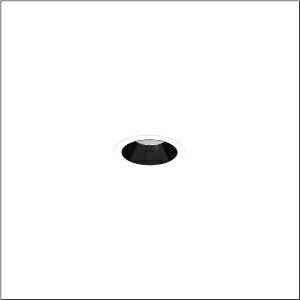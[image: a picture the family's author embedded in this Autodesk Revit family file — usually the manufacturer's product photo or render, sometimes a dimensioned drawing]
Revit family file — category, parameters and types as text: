
# Revit family: lunis_21_s_51db17ma91c
name_source: partatom
category: Lighting Fixtures
units: mm (PartAtom-declared; Revit-internal decimal feet)

## family parameters
Cut with Voids When Loaded = No
Host = Face
Light Source = No
Part Type = Normal
Room Calculation Point = No
Round Connector Dimension = Use Diameter
Shared = No

## types (1)
- --- (1 x LED, 830 lm, 5.9 W, 6500K)
    Apparent Load = 6 VA
    CIE Flux Codes = 97 100 100 100 100
    Color Rendering = 80
    Color Temperature = 6500K
    Default Elevation = 1800 mm
    Description = Lunis 21,  S, downlight, light control with lens, of PMMA, anti glare with reflector, of PC, light emission: direct distribution, LED rated luminous flux: 840lm, light colour: 830/840/865, with terminal, 3-pole, mains connection: 220..240V, AC, 50..60Hz, housing, round, of diecast aluminium, traffic white (RAL 9016), diameter: 84mm, clamping range: 1..40mm, protection rating (complete): IP20, protection rating (on room side): IP54, insulation class (complete): insulation class II (safety insulation), certification: CE, impact resistance: IK03, packaging unit: 1 piece
    Height = 0 mm  [stored 0 ft]
    Lamp = 1 x LED
    Lamp Light Flux = 830 lm
    Lamp Power = 5.9 W
    Lamp count = 1
    Length = 84 mm
    Luminous efficacy = 141 lm/W
    Manufacturer = Siteco
    ModVariant = No
    Model = 51DB17MA91C
    Mounting Place = Ceiling
    Mounting Type = Recessed
    Number of Poles = 1
    OnlyDefault = Yes
    Power Factor = 1
    Product Name = Lunis 21 S
    Product group = downlight
    ProductGroupID = 401
    Protection Class = Protection class II
    Protection Degree = IP 20
    RLX_Detail_Level = 1
    RLX_Emergency_Light_Flux = 0 lm
    RLX_Emergency_Type = 0
    RLX_Emergency_Type_DB = No
    RlxData = <blob elided: 8701 chars, md5=08a4d433>
    Socket = socket
    Standby Power = 0 W
    System Light Flux = 830 lm
    System Power = 6 W
    Type Comments = individual setting: colour temperature 6500K
    Type Image = l_1290844.jpg
    URL = http://relux.com
    VarID = @adj_040233
    Voltage = 0 V
    Weight = 0.00 kg
    Width = 0 mm  [stored 0 ft]

note: [stored X ft] marks values corroborated as IEEE doubles in the binary element streams (Revit-internal decimal feet)

## geometry (parser evidence)
native form markers: Sweep x10
no freeform markers — native parametric forms only
